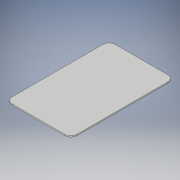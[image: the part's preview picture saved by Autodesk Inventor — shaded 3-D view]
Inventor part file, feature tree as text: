
AUTODESK INVENTOR PART (.ipt)
format: ipt  version: 2018 (Build 220112000, 112)  size: 99,328 bytes
history: native  units: in
note: dims shown in document units (in); Inventor stores cm internally (conversion verified against a paired STEP export)
features: extrude x1, fillet x1, sketch x1
ambient origin geometry x8: Origin, YZ Plane, XZ Plane, XY Plane, X Axis, Y Axis, Z Axis, Center Point
bodies: Solid1 (feature_tree)
feature tree (3):
  extrude  "Extrusion1"  Depth=2.125in
  fillet  "Fillet1"  Radius=0.0394in
  sketch  "Sketch1"  dims[d0=3.375in d1=2.125in d2=0.0394in d3=0.0in d4=0.1969in]
